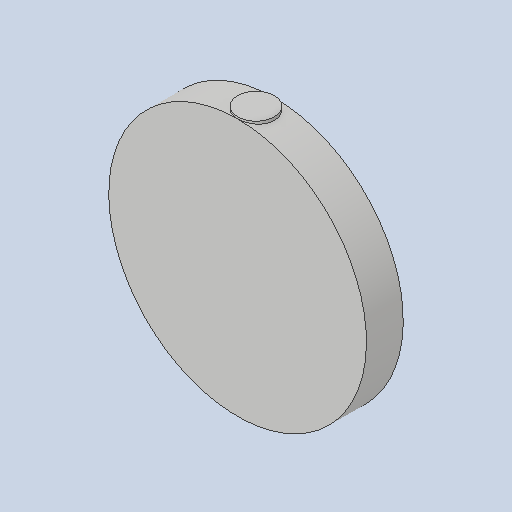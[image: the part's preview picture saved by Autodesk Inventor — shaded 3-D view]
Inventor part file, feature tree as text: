
AUTODESK INVENTOR PART (.ipt)
format: ipt  version: 2025 (Build 290162010, 162A)  size: 96,768 bytes
history: native  units: mm
features: extrude x2, sketch x2, other x1
ambient origin geometry x8: Origin, YZ Plane, XZ Plane, XY Plane, X Axis, Y Axis, Z Axis, Center Point
bodies: Body1 (feature_tree)
feature tree (5):
  other  "Твердое тело1"
  extrude  "Выдавливание1"  Depth=140.0mm
  extrude  "Выдавливание2"  Depth=20.0mm TaperAngle=0.0deg
  sketch  "Эскиз3"
  sketch  "Эскиз4"
